# Revit family: TY-B-TY1151_Metric
name_source: partatom
category: Sprinklers
units: mm (PartAtom-declared; Revit-internal decimal feet)

## family parameters
Always vertical = Yes
Cut with Voids When Loaded = No
Maintain Annotation Orientation = No
OmniClass Number = 23.65.70.17.11.24
OmniClass Title = Fire Fighting Sprinkler Heads
Part Type = Normal
Room Calculation Point = No
Round Connector Dimension = Use Diameter
Shared = No
Work Plane-Based = No

## types (24) — shared parameters
COBie = Yes
COBie.Component.Name = Sprinklers:Upright_SIN
COBie.Type = Yes
COBie.Type.AssetType = Fixed
COBie.Type.Category = Pr_70_55_97_84:Sprinklers
COBie.Type.DurationUnit = year
COBie.Type.Manufacturer = Tyco Fire Protection Products
COBie.Type.Material = Bronze
COBie.Type.Shape = Cylinder
Coverage = Standard
Coverage_ = Standard
K-Factor = 40.2544
Manufacturer = Tyco Fire Protection Products
Manufacturer URL = www.tyco-fire.com
Material_ = Bronze
Model = TY-B
Nominal Diameter 1 = 15 mm
Orifice = Standard
Orifice Size = 8 mm
Outside Diameter 1 = 21 mm
Response = Standard
Response_ = Standard
SIN No = TY1151
Takeout 1 = 56 mm
Technical Data Sheet No = TFP151
zero-valued in all types: COBie.Type.NominalHeight, COBie.Type.NominalLength, COBie.Type.NominalWidth, COBie.Type.ReplacementCost, Default Elevation, Style Id

## per-type parameters (varying)
| type | COBie.Component.Description | COBie.Type.Colour | COBie.Type.Finish | COBie.Type.ModelNumber | COBie.Type.ModelReference | COBie.Type.Size | COBie.Type.WarrantyGuarantorParts | Description | Finish_ | Part No | Temperature Rating |
| Upright 1/2" NPT 57.2°C Brass_57-530-1-135 | TY-B Wet Upright  135°F K2.8 1/2 NPT Br | Brass | Natural Brass | 57-530-1-135 | TY-B Wet Upright  135°F K2.8 1/2 NPT Br | 1/2"(DN15) | http://tycofsbp.com
TFPPTerms_of_Sale.pdf | TY-B Wet Upright 57.2°C K40.3 DN15 NPT Br | Natural Brass | 57-530-1-135 | 57 °C |
| Upright 1/2" NPT 68.3°C Brass_57-530-1-155 | TY-B Wet Upright  155°F K2.8 1/2 NPT Br | Brass | Natural Brass | 57-530-1-155 | TY-B Wet Upright  155°F K2.8 1/2 NPT Br | 1/2"(DN15) | http://tycofsbp.com
TFPPTerms_of_Sale.pdf | TY-B Wet Upright 68.3°C K40.3 DN15 NPT Br | Natural Brass | 57-530-1-155 | 68 °C |
| Upright 1/2" NPT 79.4°C Brass_57-530-1-175 | TY-B Wet Upright  175°F K2.8 1/2 NPT Br | Brass | Natural Brass | 57-530-1-175 | TY-B Wet Upright  175°F K2.8 1/2 NPT Br | 1/2"(DH15) | http://tycofsbp.com
TFPPTerms_of_Sale.pdf | TY-B Wet Upright 79.4°C K40.3 DN15 NPT Br | Natural Brass | 57-530-1-175 | 79 °C |
| Upright 1/2" NPT 93.3°C Brass_57-530-1-200 | TY-B Wet Upright  200°F K2.8 1/2 NPT Br | Brass | Natural Brass | 57-530-1-200 | TY-B Wet Upright  200°F K2.8 1/2 NPT Br | 1/2"(DN15) | http://tycofsbp.com
TFPPTerms_of_Sale.pdf | TY-B Wet Upright 93.3°C K40.3 DN15 NPT Br | Natural Brass | 57-530-1-200 | 93 °C |
| Upright 1/2" NPT 141.1°C Brass_57-530-1-286 | TY-B Wet Upright  286°F K2.8 1/2 NPT Br | Brass | Natural Brass | 57-530-1-286 | TY-B Wet Upright  286°F K2.8 1/2 NPT Br | 1/2"(DN15) | http://tycofsbp.com
TFPPTerms_of_Sale.pdf | TY-B Wet Upright 141.1°C K40.3 DN15 NPT Br | Natural Brass | 57-530-1-286 | 141 °C |
| Upright 1/2" NPT 182.2°C Brass_57-530-1-360 | TY-B Wet Upright  360°F K2.8 1/2 NPT Br | Brass | Natural Brass | 57-530-1-360 | TY-B Wet Upright  360°F K2.8 1/2 NPT Br | 1/2"(DN15) | http://tycofsbp.com
TFPPTerms_of_Sale.pdf | TY-B Wet Upright 182.2°C K40.3 DN15 NPT Br | Natural Brass | 57-530-1-360 | 182 °C |
| Upright 1/2" NPT 57.2°C Wh9010_57-530-3-135 | TY-B Wet Upright  135°F K2.8 1/2 NPT Wh9010 | White | Pure White | 57-530-3-135 | TY-B Wet Upright  135°F K2.8 1/2 NPT Wh9010 | 1/2"(DN15) | http://tycofsbp.com
TFPPTerms_of_Sale.pdf | TY-B Wet Upright 57.2°C K40.3 DN15 NPT Wh9010 | White RAL9010 | 57-530-3-135 | 57 °C |
| Upright 1/2" NPT 68.3°C Wh9010_57-530-3-155 | TY-B Wet Upright  155°F K2.8 1/2 NPT Wh9010 | White | Pure White | 57-530-3-155 | TY-B Wet Upright  155°F K2.8 1/2 NPT Wh9010 | 1/2"(DN15) | http://tycofsbp.com
TFPPTerms_of_Sale.pdf | TY-B Wet Upright 68.3°C K40.3 DN15 NPT Wh9010 | White RAL9010 | 57-530-3-155 | 68 °C |
| Upright 1/2" NPT 79.4°C  Wh9010_57-530-3-175 | TY-B Wet Upright  175°F K2.8 1/2 NPT Wh9010 | White | Pure White | 57-530-3-175 | TY-B Wet Upright  175°F K2.8 1/2 NPT Wh9010 | 1/2"(DN15) | http://tycofsbp.com
TFPPTerms_of_Sale.pdf | TY-B Wet Upright 79.4°C K40.3 DN15 NPT Wh9010 | White RAL9010 | 57-530-3-175 | 79 °C |
| Upright 1/2" NPT 93.3°C Wh9010_57-530-3-200 | TY-B Wet Upright  200°F K2.8 1/2 NPT Wh9010 | White | Pure White | 57-530-3-200 | TY-B Wet Upright  200°F K2.8 1/2 NPT Wh9010 | 1/2"(DN15) | http://tycofsbp.com
TFPPTerms_of_Sale.pdf | TY-B Wet Upright 93.3°C K40.3 DN15 NPT Wh9010 | White RAL9010 | 57-530-3-200 | 93 °C |
| Upright 1/2" NPT 141.1°C Wh9010_57-530-3-286 | TY-B Wet Upright  286°F K2.8 1/2 NPT Wh9010 | White | Pure White | 57-530-3-286 | TY-B Wet Upright  286°F K2.8 1/2 NPT Wh9010 | 1/2"(DN15) | http://tycofsbp.com
TFPPTerms_of_Sale.pdf | TY-B Wet Upright 141.1°C K40.3 DN15 NPT Wh9010 | White RAL9010 | 57-530-3-286 | 141 °C |
| Wet Upright 1/2" NPT 182.2°C Wh9010_57-530-3-360 | TY-B Wet Upright  360°F K2.8 1/2 NPT Wh9010 | White | Pure White | 57-530-3-360 | TY-B Wet Upright  360°F K2.8 1/2 NPT Wh9010 | 1/2"(DN15) | http://tycofsbp.com
TFPPTerms_of_Sale.pdf | TY-B Wet Upright 182.2°C K40.3 DN15 NPT Wh9010 | White RAL9010 | 57-530-3-360 | 182 °C |
| Upright 1/2" NPT 57.2°C Wh9003_57-530-4-135 | TY-B Wet Upright  57.2°C K40.3 DN15 NPT Wh9003 | White | Signal White | 57-530-4-135 | TY-B Wet Upright  57.2°C K40.3 DN15 NPT Wh9003 | 1/2"(DN15) | http://tycofsbp.com | TY-B Wet Upright 57.2°C K40.3 DN15 NPT Wh9003 | White RAL9003 | 57-530-4-135 | 57 °C |
| Upright 1/2" NPT 68.3°C Wh9003_57-530-4-155 | TY-B Wet Upright  68.3°C K40.3 DN15 NPT Wh9003 | White | Signal White | 57-530-4-155 | TY-B Wet Upright  68.3°C K40.3 DN15 NPT Wh9003 | 1/2"(DN15) | http://tycofsbp.com | TY-B Wet Upright 68.3°C K40.3 DN15 NPT Wh9003 | White RAL9003 | 57-530-4-155 | 68 °C |
| Upright 1/2" NPT 79.4°C  Wh9003_57-530-4-175 | TY-B Wet Upright  79.4°C K40.3 DN15 NPT Wh9003 | White | Signal White | 57-530-4-175 | TY-B Wet Upright  79.4°C K40.3 DN15 NPT Wh9003 | 1/2"(DN15) | http://tycofsbp.com | TY-B Wet Upright 79.4°C K40.3 DN15 NPT Wh9003 | White RAL9003 | 57-530-4-175 | 79 °C |
| Upright 1/2" NPT 93.3°C  Wh9003_57-530-4-200 | TY-B Wet Upright  93.3°C K40.3 DN15 NPT Wh9003 | White | Signal White | 57-530-4-200 | TY-B Wet Upright  93.3°C K40.3 DN15 NPT Wh9003 | 1/2"(DN15) | http://tycofsbp.com | TY-B Wet Upright 93.3°C K40.3 DN15 NPT Wh9003 | White RAL9003 | 57-530-4-200 | 93 °C |
| Upright 1/2" NPT 141.1°C Wh9003_57-530-4-286 | TY-B Wet Upright  141.1°C K40.3 DN15 NPT Wh9003 | White | Signal White | 57-530-4-286 | TY-B Wet Upright  141.1°C K40.3 DN15 NPT Wh9003 | 1/2"(DN15) | http://tycofsbp.com | TY-B Wet Upright 141.1°C K40.3 DN15 NPT Wh9003 | White RAL9003 | 57-530-4-286 | 141 °C |
| Wet Upright 1/2" NPT 182.2°C Wh9003_57-530-4-360 | TY-B Wet Upright  182.2°C K40.3 DN15 NPT Wh9003 | White | Signal White | 57-530-4-360 | TY-B Wet Upright  182.2°C K40.3 DN15 NPT Wh9003 | 1/2"(DN15) | http://tycofsbp.com | TY-B Wet Upright 182.2°C K40.3 DN15 NPT Wh9003 | White RAL9003 | 57-530-4-360 | 182 °C |
| Upright 1/2" NPT 57.2°C Chr_57-530-9-135 | TY-B Wet Upright  135°F K2.8 1/2 NPT Chr | Silver | Chrome Plated | 57-530-9-135 | TY-B Wet Upright  135°F K2.8 1/2 NPT Chr | 1/2"(DN15) | http://tycofsbp.com
TFPPTerms_of_Sale.pdf | TY-B Wet Upright 57.2°C K40.3 DN15 NPT Chr | Chrome Plated | 57-530-9-135 | 57 °C |
| Upright 1/2" NPT 68.3°C Chr_57-530-9-155 | TY-B Wet Upright  155°F K2.8 1/2 NPT Chr | Silver | Chrome Plated | 57-530-9-155 | TY-B Wet Upright  155°F K2.8 1/2 NPT Chr | 1/2"(DN15) | http://tycofsbp.com
TFPPTerms_of_Sale.pdf | TY-B Wet Upright 68.3°C K40.3 DN15 NPT Chr | Chrome Plated | 57-530-9-155 | 68 °C |
| Upright 1/2" NPT 79.4°C Chr_57-530-9-175 | TY-B Wet Upright  175°F K2.8 1/2 NPT Chr | Silver | Chrome Plated | 57-530-9-175 | TY-B Wet Upright  175°F K2.8 1/2 NPT Chr | 1/2"(DN15) | http://tycofsbp.com
TFPPTerms_of_Sale.pdf | TY-B Wet Upright 79.4°C K40.3 DN15 NPT Chr | Chrome Plated | 57-530-9-175 | 79 °C |
| Upright 1/2" NPT 93.3°C Chr_57-530-9-200 | TY-B Wet Upright  200°F K2.8 1/2 NPT Chr | Silver | Chrome Plated | 57-530-9-200 | TY-B Wet Upright  200°F K2.8 1/2 NPT Chr | 1/2"(DN15) | http://tycofsbp.com
TFPPTerms_of_Sale.pdf | TY-B Wet Upright 93.3°C K40.3 DN15 NPT Chr | Chrome Plated | 57-530-9-200 | 93 °C |
| Upright 1/2" NPT 141.1°C Chr_57-530-9-286 | TY-B Wet Upright  286°F K2.8 1/2 NPT Chr | Silver | Chrome Plated | 57-530-9-286 | TY-B Wet Upright  286°F K2.8 1/2 NPT Chr | 1/2"(DN15) | http://tycofsbp.com
TFPPTerms_of_Sale.pdf | TY-B Wet Upright 141.1°C K40.3 DN15 NPT Chr | Chrome Plated | 57-530-9-286 | 141 °C |
| Wet Upright 1/2" NPT 182.2°C Chr_57-530-9-360 | TY-B Wet Upright  360°F K2.8 1/2 NPT Chr | Silver | Chrome Plated | 57-530-9-360 | TY-B Wet Upright  360°F K2.8 1/2 NPT Chr | 1/2"(DN15) | http://tycofsbp.com
TFPPTerms_of_Sale.pdf | TY-B Wet Upright 182.2°C K40.3 DN15 NPT Chr | Chrome Plated | 57-530-9-360 | 182 °C |

## geometry (parser evidence)
native form markers: Blend x2, Sweep x61
no freeform markers — native parametric forms only
